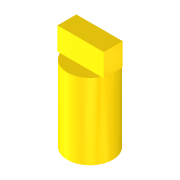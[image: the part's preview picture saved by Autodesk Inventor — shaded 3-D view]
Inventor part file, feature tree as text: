
AUTODESK INVENTOR PART (.ipt)
format: ipt  version: 2022 (Build 260153000, 153)  size: 93,184 bytes
history: native  units: mm
features: extrude x2, sketch x2
ambient origin geometry x8: Origin, YZ Plane, XZ Plane, XY Plane, X Axis, Y Axis, Z Axis, Center Point
bodies: Volumenkörper1 (feature_tree)
feature tree (4):
  extrude  "Extrusion1"  Depth=10.0mm TaperAngle=0.0deg
  extrude  "Extrusion2"  Depth=2.5mm
  sketch  "Skizze1"  dims[d0=6.0mm d1=10.0mm d2=0.0mm]
  sketch  "Skizze2"  dims[d3=6.1mm d4=2.5mm d5=3.0mm d6=0.0mm]
